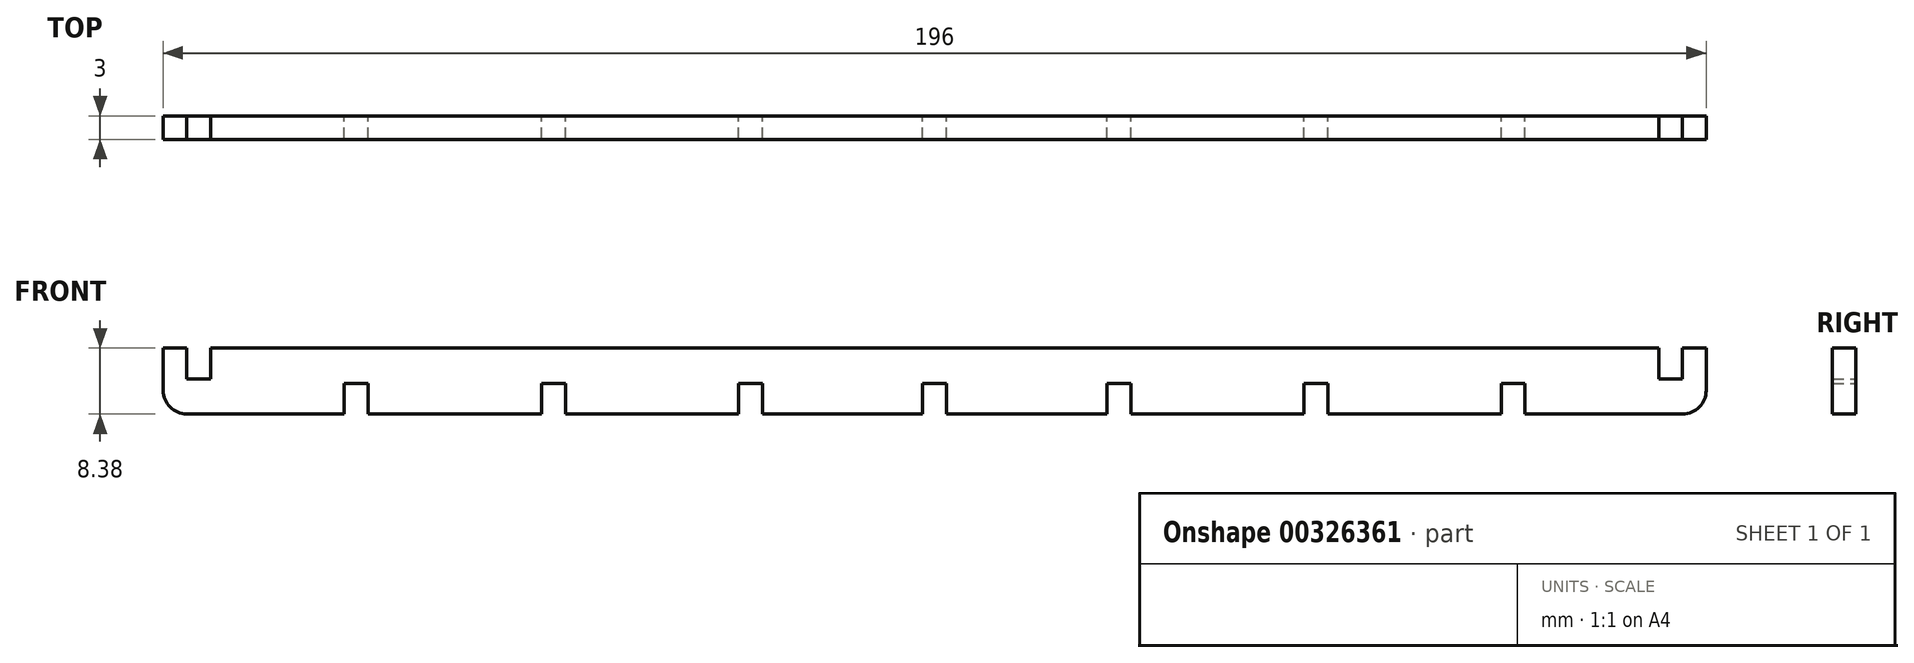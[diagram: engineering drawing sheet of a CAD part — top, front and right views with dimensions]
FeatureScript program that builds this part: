
annotation { "Feature Type Name" : "Feature", "Feature Type Description" : "" }
export const myFeature = defineFeature(function(context is Context, id is Id, definition is map)
    precondition{}
    {
        {
            var Q0;
            Q0=qCreatedBy(makeId("Front.planeOp"),FACE);
            var sketch = newSketch(context, id + "F0", { "sketchPlane" : qUnion([Q0])});
            skLineSegment(sketch, "E0", {"start": v(-71.96, 0) * mm, "end": v(-49.96, 0) * mm});
            skLineSegment(sketch, "E1", {"start": v(75, 3.9) * mm, "end": v(75, 0) * mm});
            skPoint(sketch, "E2", {"position": v(-75, 3.9) * mm});
            skLineSegment(sketch, "E3", {"start": v(-98, 8.38) * mm, "end": v(-98, 3) * mm});
            skLineSegment(sketch, "E4", {"start": v(-95, 4.48) * mm, "end": v(-91.96, 4.48) * mm});
            skLineSegment(sketch, "E5", {"start": v(-98, 8.38) * mm, "end": v(-95, 8.38) * mm});
            skLineSegment(sketch, "E6", {"start": v(-75, 3.9) * mm, "end": v(-75, 0) * mm});
            skLineSegment(sketch, "E7", {"start": v(-95, 8.38) * mm, "end": v(-95, 4.48) * mm});
            skLineSegment(sketch, "E8", {"start": v(-91.96, 4.48) * mm, "end": v(-91.96, 8.38) * mm});
            skLineSegment(sketch, "E9", {"start": v(-75, 3.9) * mm, "end": v(-71.96, 3.9) * mm});
            skLineSegment(sketch, "E10", {"start": v(-71.96, 3.9) * mm, "end": v(-71.96, 0) * mm});
            skLineSegment(sketch, "E11", {"start": v(-95, 0) * mm, "end": v(-75, 0) * mm});
            skLineSegment(sketch, "E12", {"start": v(71.96, 0) * mm, "end": v(71.96, 3.9) * mm});
            skLineSegment(sketch, "E13", {"start": v(71.96, 3.9) * mm, "end": v(75, 3.9) * mm});
            skLineSegment(sketch, "E14", {"start": v(75, 0) * mm, "end": v(95, 0) * mm});
            skLineSegment(sketch, "E15", {"start": v(98, 3) * mm, "end": v(98, 8.38) * mm});
            skLineSegment(sketch, "E16", {"start": v(98, 8.38) * mm, "end": v(95, 8.38) * mm});
            skLineSegment(sketch, "E17", {"start": v(95, 8.38) * mm, "end": v(95, 4.48) * mm});
            skLineSegment(sketch, "E18", {"start": v(95, 4.48) * mm, "end": v(91.96, 4.48) * mm});
            skLineSegment(sketch, "E19", {"start": v(91.96, 4.48) * mm, "end": v(91.96, 8.38) * mm});
            skPoint(sketch, "E20", {"position": v(-49.96, 0) * mm});
            skPoint(sketch, "E21", {"position": v(-24.92, 0) * mm});
            skPoint(sketch, "E22", {"position": v(24.92, 0) * mm});
            skPoint(sketch, "E23", {"position": v(49.96, 0) * mm});
            skLineSegment(sketch, "E24", {"start": v(-49.96, 0) * mm, "end": v(-49.96, 3.9) * mm});
            skLineSegment(sketch, "E25", {"start": v(-49.96, 3.9) * mm, "end": v(-46.92, 3.9) * mm});
            skLineSegment(sketch, "E26", {"start": v(-46.92, 3.9) * mm, "end": v(-46.92, 0) * mm});
            skLineSegment(sketch, "E27", {"start": v(-24.92, 0) * mm, "end": v(-24.92, 3.9) * mm});
            skLineSegment(sketch, "E28", {"start": v(-24.92, 3.9) * mm, "end": v(-21.88, 3.9) * mm});
            skLineSegment(sketch, "E29", {"start": v(-21.88, 3.9) * mm, "end": v(-21.88, 0) * mm});
            skLineSegment(sketch, "E30", {"start": v(24.92, 0) * mm, "end": v(24.92, 3.9) * mm});
            skLineSegment(sketch, "E31", {"start": v(24.92, 3.9) * mm, "end": v(21.88, 3.9) * mm});
            skLineSegment(sketch, "E32", {"start": v(21.88, 3.9) * mm, "end": v(21.88, 0) * mm});
            skLineSegment(sketch, "E33", {"start": v(49.96, 0) * mm, "end": v(49.96, 3.9) * mm});
            skLineSegment(sketch, "E34", {"start": v(49.96, 3.9) * mm, "end": v(46.92, 3.9) * mm});
            skLineSegment(sketch, "E35", {"start": v(46.92, 3.9) * mm, "end": v(46.92, 0) * mm});
            skPoint(sketch, "E36", {"position": v(-1.52, 0) * mm});
            skPoint(sketch, "E37", {"position": v(1.52, 0) * mm});
            skLineSegment(sketch, "E38", {"start": v(-1.52, 0) * mm, "end": v(-1.52, 3.9) * mm});
            skLineSegment(sketch, "E39", {"start": v(-1.52, 3.9) * mm, "end": v(1.52, 3.9) * mm});
            skLineSegment(sketch, "E40", {"start": v(1.52, 3.9) * mm, "end": v(1.52, 0) * mm});
            skLineSegment(sketch, "E41.trimOffspring", {"start": v(-46.92, 0) * mm, "end": v(-24.92, 0) * mm});
            skLineSegment(sketch, "E42.trimOffspring", {"start": v(-21.88, 0) * mm, "end": v(-1.52, 0) * mm});
            skLineSegment(sketch, "E43.trimOffspring", {"start": v(1.52, 0) * mm, "end": v(21.88, 0) * mm});
            skLineSegment(sketch, "E44.trimOffspring", {"start": v(24.92, 0) * mm, "end": v(46.92, 0) * mm});
            skLineSegment(sketch, "E45.trimOffspring", {"start": v(49.96, 0) * mm, "end": v(71.96, 0) * mm});
            skPoint(sketch, "E46.visualSharp", {"position": v(-98, 0) * mm});
            skArc(sketch, "E46.filletArc", {"start": v(-98, 3) * mm, "mid": v(-97.12, 0.88) * mm, "end": v(-95, 0) * mm});
            skPoint(sketch, "E47.visualSharp", {"position": v(98, 0) * mm});
            skArc(sketch, "E47.filletArc", {"start": v(95, 0) * mm, "mid": v(97.12, 0.88) * mm, "end": v(98, 3) * mm});
            skLineSegment(sketch, "E48", {"start": v(-91.96, 8.38) * mm, "end": v(91.96, 8.38) * mm});
            skSolve(sketch);
        }
        {
            var Q0;
            Q0=makeQuery(id+"F0.imprint","IMPRINT",FACE,{"disambiguationData":[TD([[makeQuery(id+"F0.imprint","IMPRINT",EDGE,{"derivedFrom":sQuery(id+"F0.wireOp",EDGE,"E0")}),1.0]])]});
            extrude(context, id + "F1", {"entities" : qUnion([Q0]), "depth" : 3 * mm});
        }
    });
